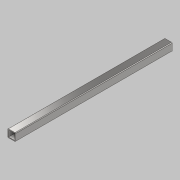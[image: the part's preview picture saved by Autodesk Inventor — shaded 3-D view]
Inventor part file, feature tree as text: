
AUTODESK INVENTOR PART (.ipt)
format: ipt  version: 2021 (Build 250183000, 183)  size: 95,744 bytes
history: native  units: mm
features: extrude x1, fillet x1, sketch x1
ambient origin geometry x8: Origin, YZ Plane, XZ Plane, XY Plane, X Axis, Y Axis, Z Axis, Center Point
bodies: Solid1 (feature_tree)
feature tree (3):
  extrude  "Extrusion1"  Depth=25.0mm
  fillet  "Fillet1"  Radius=12.5mm
  sketch  "Sketch1"  dims[d0=25.0mm d1=25.0mm d2=12.5mm d3=12.5mm d4=2.5mm d5=500.0mm d6=0.0mm d7=2.0mm]
